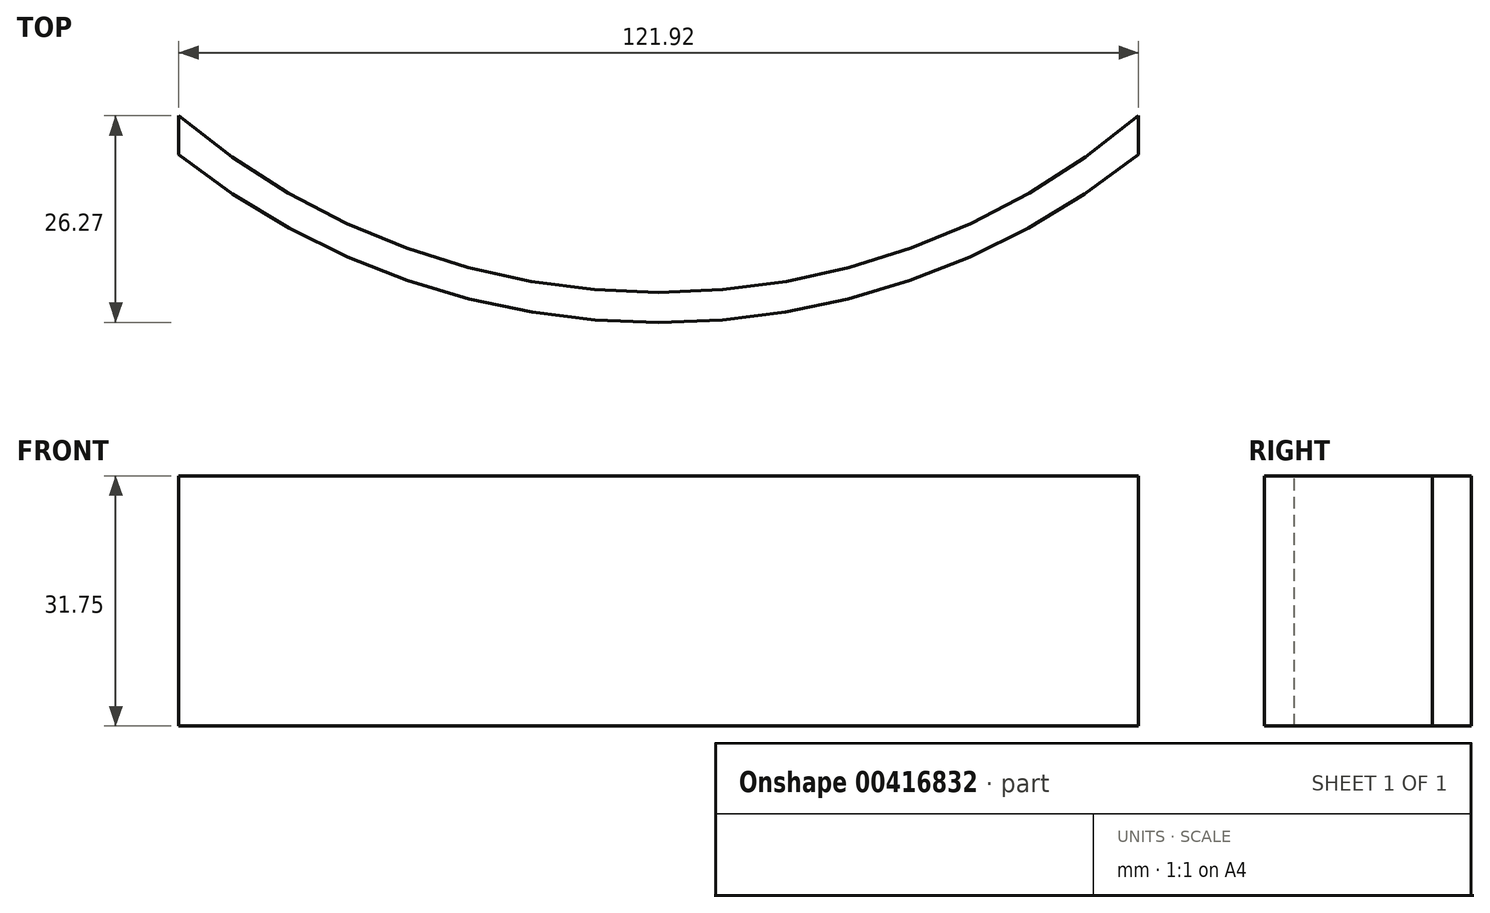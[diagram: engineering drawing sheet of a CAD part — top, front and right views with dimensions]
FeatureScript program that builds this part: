
annotation { "Feature Type Name" : "Feature", "Feature Type Description" : "" }
export const myFeature = defineFeature(function(context is Context, id is Id, definition is map)
    precondition{}
    {
        {
            var Q0;
            Q0=qCreatedBy(makeId("Top.planeOp"),FACE);
            var sketch = newSketch(context, id + "F0", { "sketchPlane" : qUnion([Q0])});
            skArc(sketch, "E0", {"start": v(-60.96, 4.77) * mm, "mid": v(0, -16.56) * mm, "end": v(60.96, 4.77) * mm});
            skArc(sketch, "E1", {"start": v(-60.96, 9.7) * mm, "mid": v(0, -12.75) * mm, "end": v(60.96, 9.7) * mm});
            skLineSegment(sketch, "E2", {"start": v(-60.96, 9.7) * mm, "end": v(-60.96, 4.77) * mm});
            skLineSegment(sketch, "E3", {"start": v(60.96, 4.77) * mm, "end": v(60.96, 9.7) * mm});
            skSolve(sketch);
        }
        {
            var Q0;
            Q0=sQuery(id+"F0.wireOp",EDGE,"E0");
            var Q1;
            Q1=sQuery(id+"F0.wireOp",EDGE,"E1");
            var Q2;
            Q2=sQuery(id+"F0.wireOp",EDGE,"E2");
            var Q3;
            Q3=sQuery(id+"F0.wireOp",EDGE,"E3");
            extrude(context, id + "F1", {"bodyType" : ToolBodyType.SURFACE, "surfaceEntities" : qUnion([Q0, Q1, Q2, Q3]), "depth" : 31.75 * mm, "offsetDistance" : 25.4 * mm});
        }
    });
